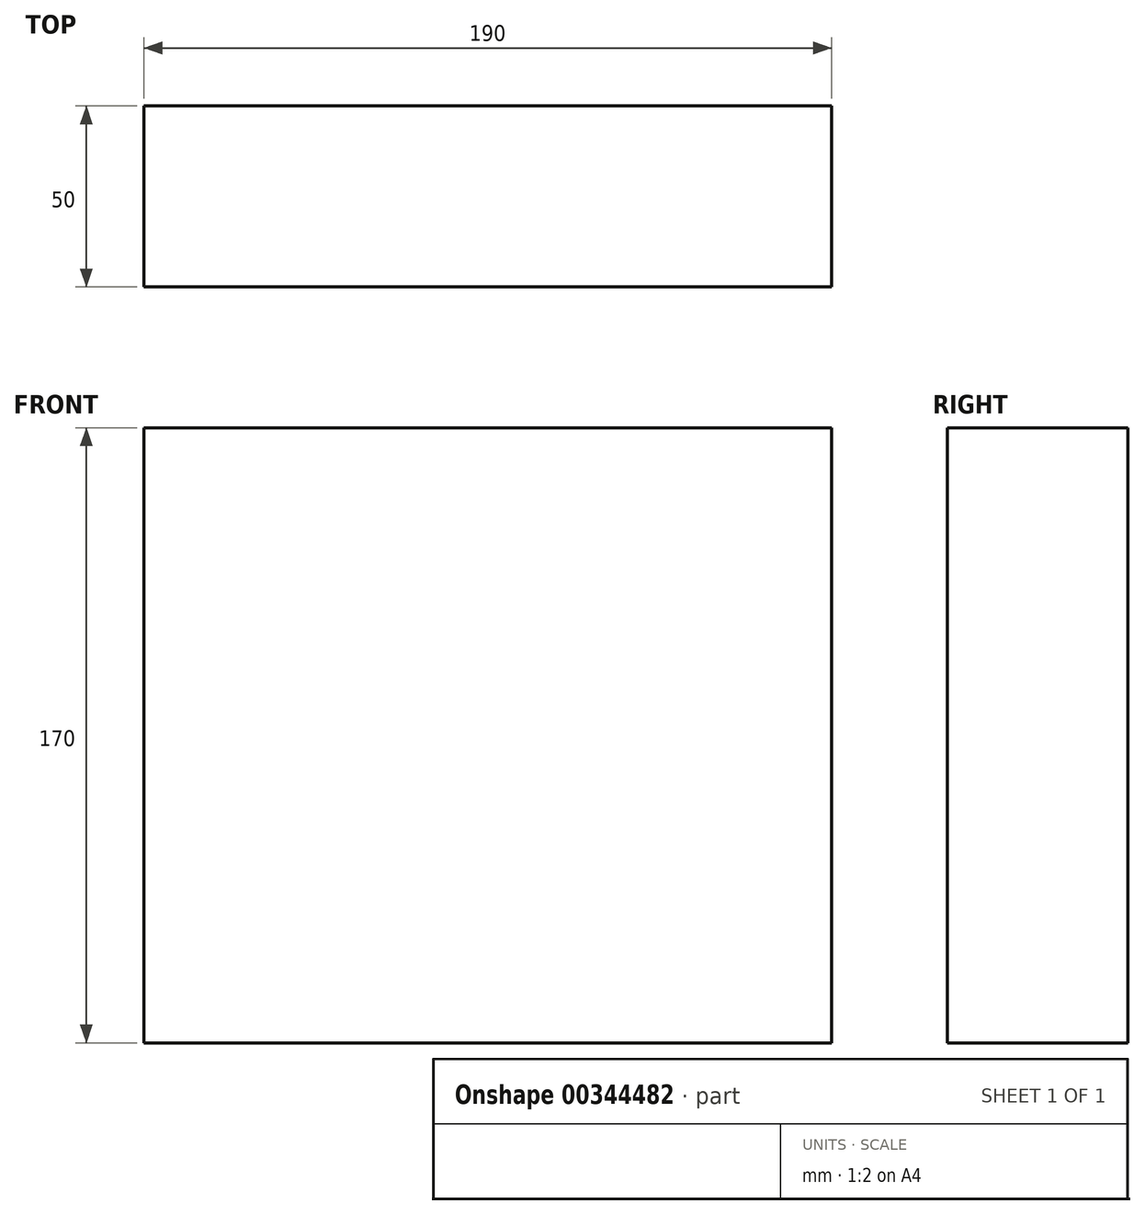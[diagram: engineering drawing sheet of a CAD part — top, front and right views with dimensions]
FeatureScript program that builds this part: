
annotation { "Feature Type Name" : "Feature", "Feature Type Description" : "" }
export const myFeature = defineFeature(function(context is Context, id is Id, definition is map)
    precondition{}
    {
        {
            var Q0;
            Q0=qCreatedBy(makeId("Front.planeOp"),FACE);
            var sketch = newSketch(context, id + "F0", { "sketchPlane" : qUnion([Q0])});
            skLineSegment(sketch, "E0.bottom", {"start": v(-30.16, 144.95) * mm, "end": v(159.84, 144.95) * mm});
            skLineSegment(sketch, "E0.top", {"start": v(-30.16, -25.05) * mm, "end": v(159.84, -25.05) * mm});
            skLineSegment(sketch, "E0.left", {"start": v(-30.16, 144.95) * mm, "end": v(-30.16, -25.05) * mm});
            skLineSegment(sketch, "E0.right", {"start": v(159.84, 144.95) * mm, "end": v(159.84, -25.05) * mm});
            skSolve(sketch);
        }
        {
            var Q0;
            Q0=makeQuery(id+"F0.imprint","IMPRINT",FACE,{"disambiguationData":[TD([[makeQuery(id+"F0.imprint","IMPRINT",EDGE,{"derivedFrom":sQuery(id+"F0.wireOp",EDGE,"E0.bottom")}),-1.0]])]});
            extrude(context, id + "F1", {"entities" : qUnion([Q0]), "depth" : 50 * mm});
        }
    });
